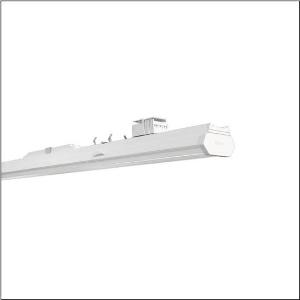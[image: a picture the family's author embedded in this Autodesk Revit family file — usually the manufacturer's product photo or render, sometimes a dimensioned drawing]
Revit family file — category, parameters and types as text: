
# Revit family: licross_r__11_protected_mo_51tp127n58xf_03c6
name_source: partatom
category: Lighting Fixtures
units: mm (PartAtom-declared; Revit-internal decimal feet)

## family parameters
Cut with Voids When Loaded = No
Host = Face
Light Source = No
Part Type = Normal
Room Calculation Point = No
Round Connector Dimension = Use Diameter
Shared = No

## types (1)
- Licross® 11 Protected MO (1 x LED, 8120 lm, 47.6 W, 5000K)
    Apparent Load = 48 VA
    CIE Flux Codes = 73 92 98 99 100
    Color Rendering = 80
    Color Temperature = 5000K
    Default Elevation = 1800 mm
    Description = Licross® 11 Protected MO, luminaire insert, of sheet steel, galvanised, coil coated, white, length: 1.500mm, width: 90mm, height: 101mm, LED rated luminous flux: 8.120lm, light colour: 850, control gear: ON/OFF, control gear: ECG, with plug, 3-pole, with phase selection, mains connection: 220..240V, AC, 50/60Hz, rated input power: 48W, halogen-free wiring, primary optical cover: cover, of PMMA, light emission: direct distribution, primary light characteristic: symmetric, protection rating (complete): IP64, insulation class (complete): insulation class I (protective earthing), certification: CE, ENEC, VDE, UKCA, protection symbol: D if used in an environment with conductive dust loads with corresponding accessories, impact resistance: IK06, permissible ambient temperature for indoor applications: -35..+45°C, reducing of maximum allowable ambient temperature of 5°C with ceiling mounting, corresponds to IFS (International Featured Standards) requirements for safety and quality in the food industry, LABS conformity tested according to VDMA 24364:2018-05, packaging unit: 1 piece
    Height = 92 mm
    Lamp = 1 x LED
    Lamp Light Flux = 8120 lm
    Lamp Power = 47.6 W
    Lamp count = 1
    Length = 1500 mm
    Luminous efficacy = 171 lm/W
    Manufacturer = Siteco
    ModVariant = No
    Model = 51TP127N58XF
    Mounting Place = Ceiling
    Mounting Type = Pendant
    Number of Poles = 1
    OnlyDefault = Yes
    Power Factor = 1
    Product Name = Licross® 11 Protected MO
    Product group = luminaire insert
    ProductGroupID = 901
    Protection Class = Protection class I
    Protection Degree = IP 64
    RLX_Detail_Level = 1
    RLX_Emergency_Light_Flux = 0 lm
    RLX_Emergency_Type = 0
    RLX_Emergency_Type_DB = No
    RlxData = <blob elided: 20629 chars, md5=d2bf5fc6>
    Socket = socket
    Standby Power = 0 W
    System Light Flux = 8120 lm
    System Power = 48 W
    Type Comments = Product without accessories
    Type Image = l_1256148.jpg
    URL = http://relux.com
    VarID = ---
    Voltage = 0 V
    Weight = 0.00 kg
    Width = 88 mm

## geometry (parser evidence)
native form markers: Blend x4, Sweep x13
no freeform markers — native parametric forms only
